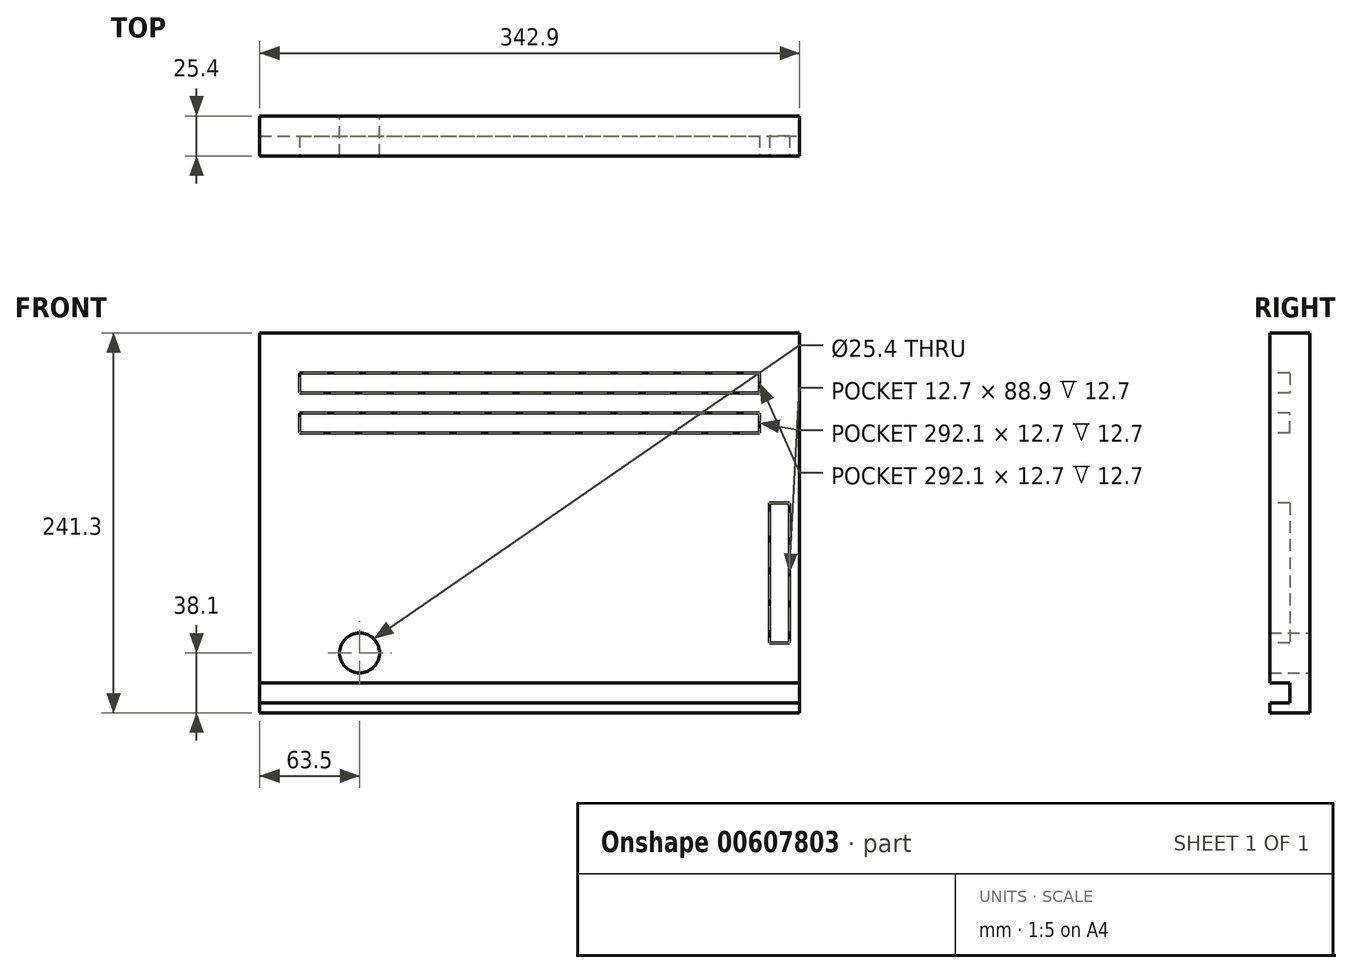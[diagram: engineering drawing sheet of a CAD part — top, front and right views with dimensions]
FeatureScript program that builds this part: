
annotation { "Feature Type Name" : "Feature", "Feature Type Description" : "" }
export const myFeature = defineFeature(function(context is Context, id is Id, definition is map)
    precondition{}
    {
        {
            var Q0;
            Q0=qCreatedBy(makeId("Front.planeOp"),FACE);
            var sketch = newSketch(context, id + "F0", { "sketchPlane" : qUnion([Q0])});
            skLineSegment(sketch, "E0.bottom", {"start": v(0, 0) * mm, "end": v(342.9, 0) * mm});
            skLineSegment(sketch, "E0.top", {"start": v(0, 177.8) * mm, "end": v(342.9, 177.8) * mm});
            skLineSegment(sketch, "E0.left", {"start": v(0, 0) * mm, "end": v(0, 177.8) * mm});
            skLineSegment(sketch, "E0.right", {"start": v(342.9, 0) * mm, "end": v(342.9, 177.8) * mm});
            skLineSegment(sketch, "E1.top", {"start": v(0, 241.3) * mm, "end": v(342.9, 241.3) * mm});
            skLineSegment(sketch, "E1.left", {"start": v(0, 177.8) * mm, "end": v(0, 241.3) * mm});
            skLineSegment(sketch, "E1.right", {"start": v(342.9, 177.8) * mm, "end": v(342.9, 241.3) * mm});
            skLineSegment(sketch, "E2", {"start": v(0, 241.3) * mm, "end": v(57.15, 241.3) * mm});
            skLineSegment(sketch, "E3.bottom", {"start": v(57.15, 241.3) * mm, "end": v(285.75, 241.3) * mm});
            skLineSegment(sketch, "E3.top", {"start": v(57.15, 457.2) * mm, "end": v(285.75, 457.2) * mm});
            skLineSegment(sketch, "E3.left", {"start": v(57.15, 241.3) * mm, "end": v(57.15, 457.2) * mm});
            skLineSegment(sketch, "E3.right", {"start": v(285.75, 241.3) * mm, "end": v(285.75, 457.2) * mm});
            skSolve(sketch);
        }
        {
            var Q0;
            Q0=makeQuery(id+"F0.imprint","IMPRINT",FACE,{"disambiguationData":[TD([[makeQuery(id+"F0.imprint","IMPRINT",EDGE,{"derivedFrom":sQuery(id+"F0.wireOp",EDGE,"E0.bottom")}),1.0]])]});
            var Q1;
            Q1=makeQuery(id+"F0.imprint","IMPRINT",FACE,{"disambiguationData":[TD([[makeQuery(id+"F0.imprint","IMPRINT",EDGE,{"derivedFrom":sQuery(id+"F0.wireOp",EDGE,"E0.top")}),1.0]])]});
            var Q2;
            Q2=makeQuery(id+"F0.imprint","IMPRINT",FACE,{"disambiguationData":[TD([[makeQuery(id+"F0.imprint","IMPRINT",EDGE,{"derivedFrom":sQuery(id+"F0.wireOp",EDGE,"E3.bottom")}),1.0]])]});
            extrude(context, id + "F1", {"entities" : qUnion([Q0, Q1, Q2]), "depth" : 25.4 * mm, "offsetDistance" : 25.4 * mm});
        }
        {
            var Q0;
            Q0=makeQuery(id+"F1.opExtrude","CAP_FACE",FACE,{"disambiguationData":[OSD([sQuery(id+"F0.wireOp",EDGE,"E0.bottom"),sQuery(id+"F0.wireOp",EDGE,"E0.top"),sQuery(id+"F0.wireOp",EDGE,"E0.left"),sQuery(id+"F0.wireOp",EDGE,"E0.right")])],"isStart":false});
            var sketch = newSketch(context, id + "F2", { "sketchPlane" : qUnion([Q0])});
            skLineSegment(sketch, "E4", {"start": v(0, 0) * mm, "end": v(0, 6.35) * mm});
            skLineSegment(sketch, "E5", {"start": v(0, 6.35) * mm, "end": v(0, 19.05) * mm});
            skLineSegment(sketch, "E6", {"start": v(0, 19.05) * mm, "end": v(342.9, 19.05) * mm});
            skLineSegment(sketch, "E7", {"start": v(342.9, 19.05) * mm, "end": v(342.9, 6.35) * mm});
            skLineSegment(sketch, "E8", {"start": v(342.9, 6.35) * mm, "end": v(0, 6.35) * mm});
            skLineSegment(sketch, "E9", {"start": v(0, 19.05) * mm, "end": v(25.4, 19.05) * mm});
            skLineSegment(sketch, "E10", {"start": v(25.4, 19.05) * mm, "end": v(25.4, 6.35) * mm});
            skLineSegment(sketch, "E11", {"start": v(25.4, 6.35) * mm, "end": v(342.9, 6.35) * mm});
            skLineSegment(sketch, "E12", {"start": v(342.9, 19.05) * mm, "end": v(330.2, 19.05) * mm});
            skLineSegment(sketch, "E13", {"start": v(330.2, 19.05) * mm, "end": v(330.2, 6.35) * mm});
            skSolve(sketch);
        }
        {
            var Q0;
            Q0=makeQuery(id+"F2.imprint","IMPRINT",FACE,{"disambiguationData":[TD([[makeQuery(id+"F2.imprint","IMPRINT",EDGE,{"derivedFrom":sQuery(id+"F2.wireOp",EDGE,"E6")}),-1.0]])]});
            extrude(context, id + "F3", {"entities" : qUnion([Q0]), "operationType" : NewBodyOperationType.REMOVE, "oppositeDirection" : true, "depth" : 12.7 * mm, "offsetDistance" : 25.4 * mm});
        }
        {
            var Q0;
            Q0=makeQuery(id+"F1.opExtrude","CAP_FACE",FACE,{"disambiguationData":[OSD([sQuery(id+"F0.wireOp",EDGE,"E0.bottom"),sQuery(id+"F0.wireOp",EDGE,"E0.top"),sQuery(id+"F0.wireOp",EDGE,"E0.left"),sQuery(id+"F0.wireOp",EDGE,"E0.right")])],"isStart":false});
            var sketch = newSketch(context, id + "F4", { "sketchPlane" : qUnion([Q0])});
            skLineSegment(sketch, "E14", {"start": v(0, 0) * mm, "end": v(0, -6.35) * mm});
            skLineSegment(sketch, "E15", {"start": v(0, -6.35) * mm, "end": v(0, -19.05) * mm});
            skLineSegment(sketch, "E16", {"start": v(0, -19.05) * mm, "end": v(342.9, -19.05) * mm});
            skLineSegment(sketch, "E17", {"start": v(342.9, -19.05) * mm, "end": v(342.9, -6.35) * mm});
            skLineSegment(sketch, "E18", {"start": v(342.9, -6.35) * mm, "end": v(0, -6.35) * mm});
            skLineSegment(sketch, "E19", {"start": v(0, -19.05) * mm, "end": v(25.4, -19.05) * mm});
            skLineSegment(sketch, "E20", {"start": v(25.4, -19.05) * mm, "end": v(25.4, -6.35) * mm});
            skLineSegment(sketch, "E21", {"start": v(25.4, -6.35) * mm, "end": v(342.9, -6.35) * mm});
            skLineSegment(sketch, "E22", {"start": v(342.9, -6.35) * mm, "end": v(330.2, -6.35) * mm});
            skLineSegment(sketch, "E23", {"start": v(330.2, -6.35) * mm, "end": v(330.2, -19.05) * mm});
            skSolve(sketch);
        }
        {
            var Q0;
            {var subQ0=sQuery(id+"F4.wireOp",EDGE,"E20");Q0=makeQuery(id+"F4.imprint","IMPRINT",FACE,{"disambiguationData":[TD([[makeQuery(id+"F4.imprint","IMPRINT",EDGE,{"derivedFrom":subQ0}),-1.0]])]});}
            extrude(context, id + "F5", {"entities" : qUnion([Q0]), "operationType" : NewBodyOperationType.REMOVE, "oppositeDirection" : true, "depth" : 12.7 * mm, "offsetDistance" : 25.4 * mm});
        }
        {
            var Q0;
            Q0=makeQuery(id+"F1.opExtrude","CAP_FACE",FACE,{"disambiguationData":[OSD([sQuery(id+"F0.wireOp",EDGE,"E0.bottom"),sQuery(id+"F0.wireOp",EDGE,"E0.top"),sQuery(id+"F0.wireOp",EDGE,"E0.left"),sQuery(id+"F0.wireOp",EDGE,"E0.right")])],"isStart":true});
            var sketch = newSketch(context, id + "F6", { "sketchPlane" : qUnion([Q0])});
            skCircle(sketch, "E24", {"center": v(-63.5, 38.1) * mm, "radius": 12.7 * mm});
            skSolve(sketch);
        }
        {
            var Q0;
            Q0=makeQuery(id+"F6.imprint","IMPRINT",FACE,{"disambiguationData":[TD([[makeQuery(id+"F6.imprint","IMPRINT",EDGE,{"derivedFrom":sQuery(id+"F6.wireOp",EDGE,"E24")}),1.0]])]});
            extrude(context, id + "F7", {"entities" : qUnion([Q0]), "operationType" : NewBodyOperationType.REMOVE, "oppositeDirection" : true, "depth" : 25.4 * mm, "offsetDistance" : 25.4 * mm});
        }
        {
            var Q0;
            Q0=makeQuery(id+"F1.opExtrude","CAP_FACE",FACE,{"disambiguationData":[OSD([sQuery(id+"F0.wireOp",EDGE,"E0.bottom"),sQuery(id+"F0.wireOp",EDGE,"E0.top"),sQuery(id+"F0.wireOp",EDGE,"E0.left"),sQuery(id+"F0.wireOp",EDGE,"E0.right")])],"isStart":false});
            var sketch = newSketch(context, id + "F8", { "sketchPlane" : qUnion([Q0])});
            skLineSegment(sketch, "E25", {"start": v(330.2, 19.05) * mm, "end": v(330.2, 44.45) * mm});
            skLineSegment(sketch, "E26", {"start": v(330.2, 44.45) * mm, "end": v(323.85, 44.45) * mm});
            skLineSegment(sketch, "E27.bottom", {"start": v(336.55, 133.35) * mm, "end": v(323.85, 133.35) * mm});
            skLineSegment(sketch, "E27.top", {"start": v(336.55, 44.45) * mm, "end": v(323.85, 44.45) * mm});
            skLineSegment(sketch, "E27.left", {"start": v(336.55, 133.35) * mm, "end": v(336.55, 44.45) * mm});
            skLineSegment(sketch, "E27.right", {"start": v(323.85, 133.35) * mm, "end": v(323.85, 44.45) * mm});
            skSolve(sketch);
        }
        {
            var Q0;
            Q0=makeQuery(id+"F8.imprint","IMPRINT",FACE,{"disambiguationData":[TD([[makeQuery(id+"F8.imprint","IMPRINT",EDGE,{"derivedFrom":sQuery(id+"F8.wireOp",EDGE,"E27.bottom")}),1.0]])]});
            extrude(context, id + "F9", {"entities" : qUnion([Q0]), "operationType" : NewBodyOperationType.REMOVE, "oppositeDirection" : true, "depth" : 12.7 * mm, "offsetDistance" : 25.4 * mm});
        }
        {
            var Q0;
            Q0=makeQuery(id+"F1.opExtrude","CAP_FACE",FACE,{"disambiguationData":[OSD([sQuery(id+"F0.wireOp",EDGE,"E0.bottom"),sQuery(id+"F0.wireOp",EDGE,"E0.left"),sQuery(id+"F0.wireOp",EDGE,"E0.right"),sQuery(id+"F0.wireOp",EDGE,"E1.top"),sQuery(id+"F0.wireOp",EDGE,"E1.left"),sQuery(id+"F0.wireOp",EDGE,"E1.right"),sQuery(id+"F0.wireOp",EDGE,"E2"),sQuery(id+"F0.wireOp",EDGE,"E3.top"),sQuery(id+"F0.wireOp",EDGE,"E3.left"),sQuery(id+"F0.wireOp",EDGE,"E3.right")])],"isStart":false});
            var sketch = newSketch(context, id + "F10", { "sketchPlane" : qUnion([Q0])});
            skLineSegment(sketch, "E28.bottom", {"start": v(285.75, 457.2) * mm, "end": v(266.7, 457.2) * mm});
            skLineSegment(sketch, "E28.top", {"start": v(285.75, 241.3) * mm, "end": v(266.7, 241.3) * mm});
            skLineSegment(sketch, "E28.left", {"start": v(285.75, 457.2) * mm, "end": v(285.75, 241.3) * mm});
            skLineSegment(sketch, "E28.right", {"start": v(266.7, 457.2) * mm, "end": v(266.7, 241.3) * mm});
            skLineSegment(sketch, "E29.bottom", {"start": v(57.15, 457.2) * mm, "end": v(76.2, 457.2) * mm});
            skLineSegment(sketch, "E29.top", {"start": v(57.15, 241.3) * mm, "end": v(76.2, 241.3) * mm});
            skLineSegment(sketch, "E29.left", {"start": v(57.15, 457.2) * mm, "end": v(57.15, 241.3) * mm});
            skLineSegment(sketch, "E29.right", {"start": v(76.2, 457.2) * mm, "end": v(76.2, 241.3) * mm});
            skLineSegment(sketch, "E30.bottom", {"start": v(76.2, 457.2) * mm, "end": v(266.7, 457.2) * mm});
            skLineSegment(sketch, "E30.top", {"start": v(76.2, 438.15) * mm, "end": v(266.7, 438.15) * mm});
            skLineSegment(sketch, "E30.left", {"start": v(76.2, 457.2) * mm, "end": v(76.2, 438.15) * mm});
            skLineSegment(sketch, "E30.right", {"start": v(266.7, 457.2) * mm, "end": v(266.7, 438.15) * mm});
            skSolve(sketch);
        }
        {
            var Q0;
            Q0=makeQuery(id+"F10.imprint","IMPRINT",FACE,{"disambiguationData":[TD([[makeQuery(id+"F10.imprint","IMPRINT",EDGE,{"derivedFrom":sQuery(id+"F10.wireOp",EDGE,"E30.bottom")}),-1.0]])]});
            var Q1;
            Q1=makeQuery(id+"F10.imprint","IMPRINT",FACE,{"disambiguationData":[TD([[makeQuery(id+"F10.imprint","IMPRINT",EDGE,{"derivedFrom":sQuery(id+"F10.wireOp",EDGE,"E29.bottom")}),-1.0]])]});
            var Q2;
            Q2=makeQuery(id+"F10.imprint","IMPRINT",FACE,{"disambiguationData":[TD([[makeQuery(id+"F10.imprint","IMPRINT",EDGE,{"derivedFrom":sQuery(id+"F10.wireOp",EDGE,"E28.bottom")}),-1.0]])]});
            extrude(context, id + "F11", {"entities" : qUnion([Q0, Q1, Q2]), "operationType" : NewBodyOperationType.REMOVE, "oppositeDirection" : true, "depth" : 12.7 * mm, "offsetDistance" : 25.4 * mm});
        }
        {
            var Q0;
            Q0=makeQuery(id+"F1.opExtrude","CAP_FACE",FACE,{"disambiguationData":[OSD([sQuery(id+"F0.wireOp",EDGE,"E0.bottom"),sQuery(id+"F0.wireOp",EDGE,"E0.left"),sQuery(id+"F0.wireOp",EDGE,"E0.right"),sQuery(id+"F0.wireOp",EDGE,"E1.top"),sQuery(id+"F0.wireOp",EDGE,"E1.left"),sQuery(id+"F0.wireOp",EDGE,"E1.right"),sQuery(id+"F0.wireOp",EDGE,"E2"),sQuery(id+"F0.wireOp",EDGE,"E3.top"),sQuery(id+"F0.wireOp",EDGE,"E3.left"),sQuery(id+"F0.wireOp",EDGE,"E3.right")])],"isStart":false});
            var sketch = newSketch(context, id + "F12", { "sketchPlane" : qUnion([Q0])});
            skLineSegment(sketch, "E31", {"start": v(0, 241.3) * mm, "end": v(0, 215.9) * mm});
            skLineSegment(sketch, "E32", {"start": v(0, 215.9) * mm, "end": v(25.4, 215.9) * mm});
            skLineSegment(sketch, "E33", {"start": v(25.4, 215.9) * mm, "end": v(317.5, 215.9) * mm});
            skLineSegment(sketch, "E34", {"start": v(317.5, 215.9) * mm, "end": v(317.5, 203.2) * mm});
            skLineSegment(sketch, "E35", {"start": v(317.5, 203.2) * mm, "end": v(25.4, 203.2) * mm});
            skLineSegment(sketch, "E36", {"start": v(25.4, 203.2) * mm, "end": v(25.4, 215.9) * mm});
            skLineSegment(sketch, "E37", {"start": v(25.4, 203.2) * mm, "end": v(25.4, 190.5) * mm});
            skLineSegment(sketch, "E38", {"start": v(25.4, 190.5) * mm, "end": v(317.5, 190.5) * mm});
            skLineSegment(sketch, "E39", {"start": v(317.5, 190.5) * mm, "end": v(317.5, 177.8) * mm});
            skLineSegment(sketch, "E40", {"start": v(317.5, 177.8) * mm, "end": v(25.4, 177.8) * mm});
            skLineSegment(sketch, "E41", {"start": v(25.4, 177.8) * mm, "end": v(25.4, 190.5) * mm});
            skSolve(sketch);
        }
        {
            var Q0;
            Q0=makeQuery(id+"F12.imprint","IMPRINT",FACE,{"disambiguationData":[TD([[makeQuery(id+"F12.imprint","IMPRINT",EDGE,{"derivedFrom":sQuery(id+"F12.wireOp",EDGE,"E33")}),-1.0]])]});
            var Q1;
            Q1=makeQuery(id+"F12.imprint","IMPRINT",FACE,{"disambiguationData":[TD([[makeQuery(id+"F12.imprint","IMPRINT",EDGE,{"derivedFrom":sQuery(id+"F12.wireOp",EDGE,"E38")}),-1.0]])]});
            extrude(context, id + "F13", {"entities" : qUnion([Q0, Q1]), "operationType" : NewBodyOperationType.REMOVE, "oppositeDirection" : true, "depth" : 12.7 * mm, "offsetDistance" : 25.4 * mm});
        }
    });
